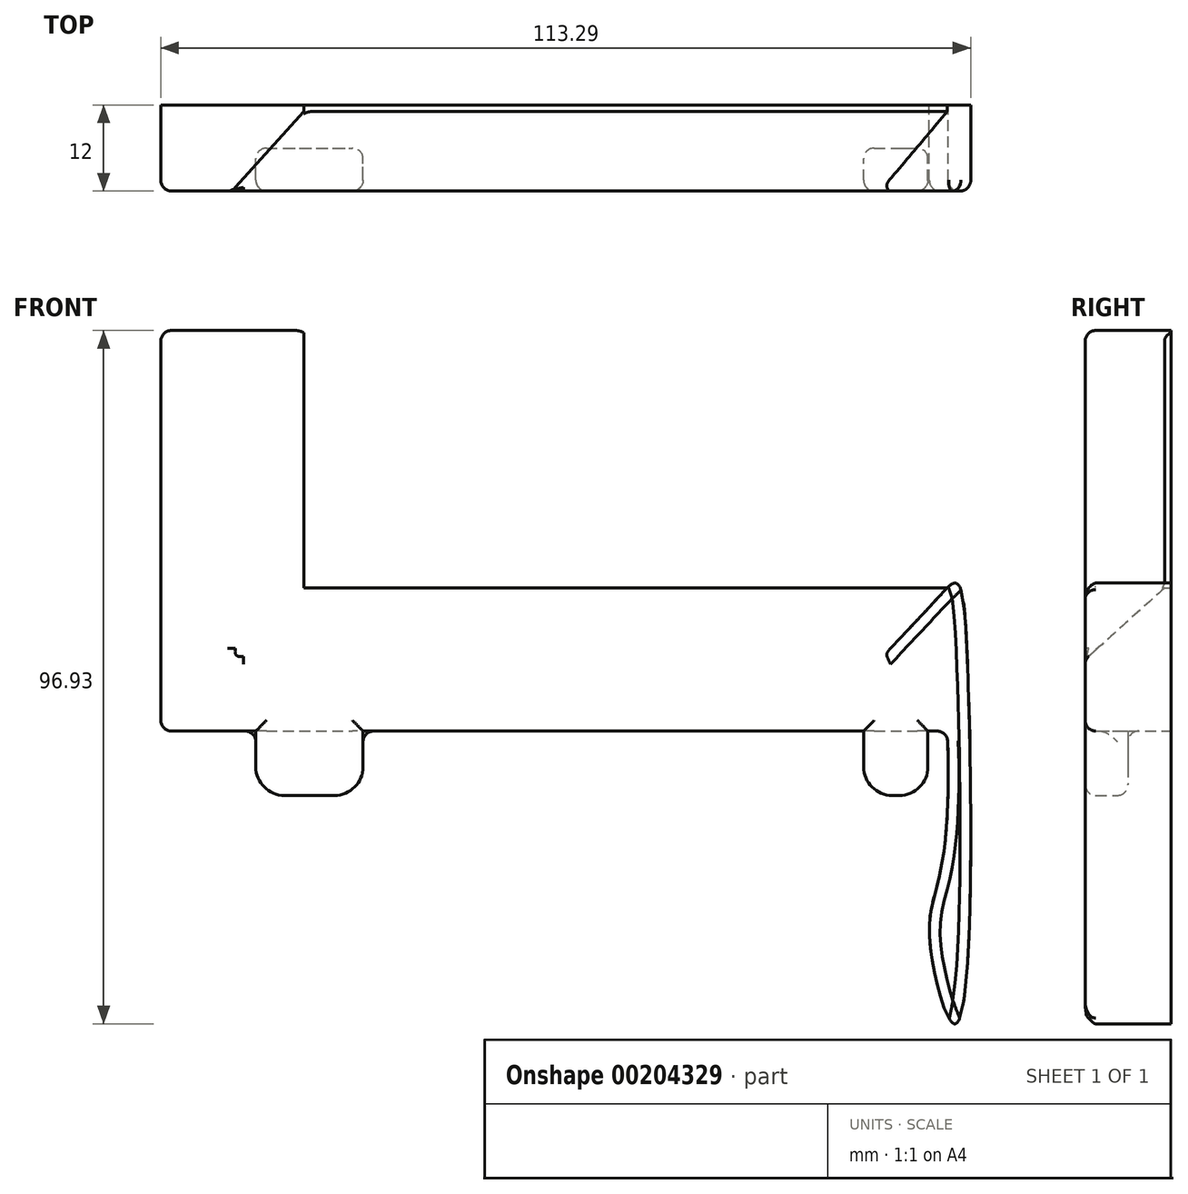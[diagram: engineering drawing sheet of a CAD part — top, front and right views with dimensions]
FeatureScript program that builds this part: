
annotation { "Feature Type Name" : "Feature", "Feature Type Description" : "" }
export const myFeature = defineFeature(function(context is Context, id is Id, definition is map)
    precondition{}
    {
        {
            var Q0;
            Q0=qCreatedBy(makeId("Front.planeOp"),FACE);
            var sketch = newSketch(context, id + "F0", { "sketchPlane" : qUnion([Q0])});
            skLineSegment(sketch, "E0", {"start": v(-34.63, 49.53) * mm, "end": v(-34.63, -6.47) * mm});
            skLineSegment(sketch, "E1", {"start": v(-34.63, -6.47) * mm, "end": v(75.37, -6.47) * mm});
            skLineSegment(sketch, "E2", {"start": v(75.37, -6.47) * mm, "end": v(75.37, 13.53) * mm});
            skLineSegment(sketch, "E3", {"start": v(75.37, 13.53) * mm, "end": v(-14.63, 13.53) * mm});
            skLineSegment(sketch, "E4", {"start": v(-14.63, 13.53) * mm, "end": v(-14.63, 49.53) * mm});
            skLineSegment(sketch, "E5", {"start": v(-14.63, 49.53) * mm, "end": v(-34.63, 49.53) * mm});
            skLineSegment(sketch, "E6", {"start": v(-21.33, -6.47) * mm, "end": v(-21.33, -15.47) * mm});
            skLineSegment(sketch, "E7", {"start": v(-21.33, -15.47) * mm, "end": v(-6.33, -15.47) * mm});
            skLineSegment(sketch, "E8", {"start": v(-6.33, -15.47) * mm, "end": v(-6.33, -6.47) * mm});
            skLineSegment(sketch, "E9", {"start": v(72.67, -6.47) * mm, "end": v(72.67, -15.47) * mm});
            skLineSegment(sketch, "E10", {"start": v(63.67, -15.47) * mm, "end": v(72.67, -15.47) * mm});
            skLineSegment(sketch, "E11", {"start": v(63.67, -15.47) * mm, "end": v(63.67, -6.47) * mm});
            skLineSegment(sketch, "E12.bottom", {"start": v(-16.83, -6.47) * mm, "end": v(-10.83, -6.47) * mm});
            skLineSegment(sketch, "E12.top", {"start": v(-16.83, -15.47) * mm, "end": v(-10.83, -15.47) * mm});
            skLineSegment(sketch, "E12.left", {"start": v(-16.83, -6.47) * mm, "end": v(-16.83, -15.47) * mm});
            skLineSegment(sketch, "E12.right", {"start": v(-10.83, -6.47) * mm, "end": v(-10.83, -15.47) * mm});
            skLineSegment(sketch, "E13.bottom", {"start": v(65.17, -6.47) * mm, "end": v(71.17, -6.47) * mm});
            skLineSegment(sketch, "E13.top", {"start": v(65.17, -15.47) * mm, "end": v(71.17, -15.47) * mm});
            skLineSegment(sketch, "E13.left", {"start": v(65.17, -6.47) * mm, "end": v(65.17, -15.47) * mm});
            skLineSegment(sketch, "E13.right", {"start": v(71.17, -6.47) * mm, "end": v(71.17, -15.47) * mm});
            skLineSegment(sketch, "E14.bottom", {"start": v(-21.33, -6.47) * mm, "end": v(-6.33, -6.47) * mm});
            skLineSegment(sketch, "E14.top", {"start": v(-21.33, -10.67) * mm, "end": v(-6.33, -10.67) * mm});
            skLineSegment(sketch, "E14.left", {"start": v(-21.33, -6.47) * mm, "end": v(-21.33, -10.67) * mm});
            skLineSegment(sketch, "E14.right", {"start": v(-6.33, -6.47) * mm, "end": v(-6.33, -10.67) * mm});
            skLineSegment(sketch, "E15.bottom", {"start": v(63.67, -6.47) * mm, "end": v(72.67, -6.47) * mm});
            skLineSegment(sketch, "E15.top", {"start": v(63.67, -10.67) * mm, "end": v(72.67, -10.67) * mm});
            skLineSegment(sketch, "E15.left", {"start": v(63.67, -6.47) * mm, "end": v(63.67, -10.67) * mm});
            skLineSegment(sketch, "E15.right", {"start": v(72.67, -6.47) * mm, "end": v(72.67, -10.67) * mm});
            skFitSpline(sketch, "E16", {"points": [v(75.37, 13.53) * mm, v(78.02, 6.78) * mm, v(76.56, -47.38) * mm, v(72.89, -35.3) * mm, v(75.37, -6.47) * mm], "startDerivative": vector(42.22, 45.02) * mm, "endDerivative": vector(-9.37, 234.27) * mm});
            skSolve(sketch);
        }
        {
            var Q0;
            {var subQ4=sQuery(id+"F0.wireOp",EDGE,"E0");Q0=makeQuery(id+"F0.imprint","IMPRINT",FACE,{"disambiguationData":[TD([[makeQuery(id+"F0.imprint","IMPRINT",EDGE,{"derivedFrom":subQ4}),1.0]])]});}
            var Q1;
            {var subQ0=sQuery(id+"F0.wireOp",EDGE,"E6");Q1=makeQuery(id+"F0.imprint","IMPRINT",FACE,{"disambiguationData":[TD([[makeQuery(id+"F0.imprint","IMPRINT",EDGE,{"derivedFrom":subQ0}),1.0]])]});}
            var Q2;
            {var subQ0=sQuery(id+"F0.wireOp",EDGE,"E9");Q2=makeQuery(id+"F0.imprint","IMPRINT",FACE,{"disambiguationData":[TD([[makeQuery(id+"F0.imprint","IMPRINT",EDGE,{"derivedFrom":subQ0}),-1.0]])]});}
            var Q3;
            Q3=makeQuery(id+"F0.imprint","IMPRINT",FACE,{"disambiguationData":[TD([[makeQuery(id+"F0.imprint","IMPRINT",EDGE,{"derivedFrom":sQuery(id+"F0.wireOp",EDGE,"E12.bottom")}),-1.0]])]});
            var Q4;
            Q4=makeQuery(id+"F0.imprint","IMPRINT",FACE,{"disambiguationData":[TD([[makeQuery(id+"F0.imprint","IMPRINT",EDGE,{"derivedFrom":sQuery(id+"F0.wireOp",EDGE,"E13.bottom")}),-1.0]])]});
            var Q5;
            {var subQ0=sQuery(id+"F0.wireOp",EDGE,"E8");Q5=makeQuery(id+"F0.imprint","IMPRINT",FACE,{"disambiguationData":[TD([[makeQuery(id+"F0.imprint","IMPRINT",EDGE,{"derivedFrom":subQ0}),1.0]])]});}
            var Q6;
            {var subQ0=sQuery(id+"F0.wireOp",EDGE,"E11");Q6=makeQuery(id+"F0.imprint","IMPRINT",FACE,{"disambiguationData":[TD([[makeQuery(id+"F0.imprint","IMPRINT",EDGE,{"derivedFrom":subQ0}),-1.0]])]});}
            var Q7;
            {var subQ0=sQuery(id+"F0.wireOp",EDGE,"E14.bottom");var subQ1=sQuery(id+"F0.wireOp",EDGE,"E12.left");var subQ2=makeQuery(id+"F0.imprint","INTERSECT",VERTEX,{"derivedFrom":[subQ1,subQ0]});Q7=makeQuery(id+"F0.imprint","IMPRINT",FACE,{"disambiguationData":[TD([[makeQuery(id+"F0.imprint","IMPRINT",EDGE,{"disambiguationData":[TD([[subQ2,-1.0]])],"derivedFrom":subQ1}),1.0]])]});}
            var Q8;
            {var subQ0=sQuery(id+"F0.wireOp",EDGE,"E12.top");Q8=makeQuery(id+"F0.imprint","IMPRINT",FACE,{"disambiguationData":[TD([[makeQuery(id+"F0.imprint","IMPRINT",EDGE,{"derivedFrom":subQ0}),1.0]])]});}
            var Q9;
            {var subQ5=sQuery(id+"F0.wireOp",EDGE,"E14.right");Q9=makeQuery(id+"F0.imprint","IMPRINT",FACE,{"disambiguationData":[TD([[makeQuery(id+"F0.imprint","IMPRINT",EDGE,{"derivedFrom":subQ5}),-1.0]])]});}
            var Q10;
            {var subQ5=sQuery(id+"F0.wireOp",EDGE,"E14.left");Q10=makeQuery(id+"F0.imprint","IMPRINT",FACE,{"disambiguationData":[TD([[makeQuery(id+"F0.imprint","IMPRINT",EDGE,{"derivedFrom":subQ5}),1.0]])]});}
            var Q11;
            {var subQ0=sQuery(id+"F0.wireOp",EDGE,"E15.bottom");var subQ1=sQuery(id+"F0.wireOp",EDGE,"E13.left");var subQ2=makeQuery(id+"F0.imprint","INTERSECT",VERTEX,{"derivedFrom":[subQ1,subQ0]});Q11=makeQuery(id+"F0.imprint","IMPRINT",FACE,{"disambiguationData":[TD([[makeQuery(id+"F0.imprint","IMPRINT",EDGE,{"disambiguationData":[TD([[subQ2,-1.0]])],"derivedFrom":subQ1}),1.0]])]});}
            var Q12;
            {var subQ0=sQuery(id+"F0.wireOp",EDGE,"E13.top");Q12=makeQuery(id+"F0.imprint","IMPRINT",FACE,{"disambiguationData":[TD([[makeQuery(id+"F0.imprint","IMPRINT",EDGE,{"derivedFrom":subQ0}),1.0]])]});}
            var Q13;
            {var subQ5=sQuery(id+"F0.wireOp",EDGE,"E15.right");Q13=makeQuery(id+"F0.imprint","IMPRINT",FACE,{"disambiguationData":[TD([[makeQuery(id+"F0.imprint","IMPRINT",EDGE,{"derivedFrom":subQ5}),-1.0]])]});}
            var Q14;
            {var subQ5=sQuery(id+"F0.wireOp",EDGE,"E15.left");Q14=makeQuery(id+"F0.imprint","IMPRINT",FACE,{"disambiguationData":[TD([[makeQuery(id+"F0.imprint","IMPRINT",EDGE,{"derivedFrom":subQ5}),1.0]])]});}
            var Q15;
            Q15=makeQuery(id+"F0.imprint","IMPRINT",FACE,{"disambiguationData":[TD([[makeQuery(id+"F0.imprint","IMPRINT",EDGE,{"derivedFrom":sQuery(id+"F0.wireOp",EDGE,"E2")}),-1.0]])]});
            extrude(context, id + "F1", {"entities" : qUnion([Q0, Q1, Q2, Q3, Q4, Q5, Q6, Q7, Q8, Q9, Q10, Q11, Q12, Q13, Q14, Q15]), "depth" : 12 * mm});
        }
        {
            var Q0;
            Q0=makeQuery(id+"F1.opExtrude","CAP_EDGE",EDGE,{"disambiguationData":[OSD([sQuery(id+"F0.wireOp",EDGE,"E4")])],"isStart":false});
            var Q1;
            Q1=makeQuery(id+"F1.opExtrude","CAP_EDGE",EDGE,{"disambiguationData":[OSD([sQuery(id+"F0.wireOp",EDGE,"E3")])],"isStart":false});
            chamfer(context, id + "F2", {"entities" : qUnion([Q0, Q1]), "chamferType" : ChamferType.OFFSET_ANGLE, "width" : 10 * mm, "oppositeDirection" : false, "angle" : 48 * degree});
        }
        {
            var Q0;
            {var subQ0=sQuery(id+"F0.wireOp",EDGE,"E12.top");Q0=makeQuery(id+"F0.imprint","IMPRINT",FACE,{"disambiguationData":[TD([[makeQuery(id+"F0.imprint","IMPRINT",EDGE,{"derivedFrom":subQ0}),1.0]])]});}
            var Q1;
            {var subQ0=sQuery(id+"F0.wireOp",EDGE,"E15.bottom");var subQ1=sQuery(id+"F0.wireOp",EDGE,"E13.left");var subQ2=makeQuery(id+"F0.imprint","INTERSECT",VERTEX,{"derivedFrom":[subQ1,subQ0]});Q1=makeQuery(id+"F0.imprint","IMPRINT",FACE,{"disambiguationData":[TD([[makeQuery(id+"F0.imprint","IMPRINT",EDGE,{"disambiguationData":[TD([[subQ2,-1.0]])],"derivedFrom":subQ1}),1.0]])]});}
            var Q2;
            {var subQ0=sQuery(id+"F0.wireOp",EDGE,"E14.bottom");var subQ1=sQuery(id+"F0.wireOp",EDGE,"E12.left");var subQ2=makeQuery(id+"F0.imprint","INTERSECT",VERTEX,{"derivedFrom":[subQ1,subQ0]});Q2=makeQuery(id+"F0.imprint","IMPRINT",FACE,{"disambiguationData":[TD([[makeQuery(id+"F0.imprint","IMPRINT",EDGE,{"disambiguationData":[TD([[subQ2,-1.0]])],"derivedFrom":subQ1}),1.0]])]});}
            var Q3;
            {var subQ5=sQuery(id+"F0.wireOp",EDGE,"E14.left");Q3=makeQuery(id+"F0.imprint","IMPRINT",FACE,{"disambiguationData":[TD([[makeQuery(id+"F0.imprint","IMPRINT",EDGE,{"derivedFrom":subQ5}),1.0]])]});}
            var Q4;
            {var subQ5=sQuery(id+"F0.wireOp",EDGE,"E14.right");Q4=makeQuery(id+"F0.imprint","IMPRINT",FACE,{"disambiguationData":[TD([[makeQuery(id+"F0.imprint","IMPRINT",EDGE,{"derivedFrom":subQ5}),-1.0]])]});}
            var Q5;
            {var subQ5=sQuery(id+"F0.wireOp",EDGE,"E15.left");Q5=makeQuery(id+"F0.imprint","IMPRINT",FACE,{"disambiguationData":[TD([[makeQuery(id+"F0.imprint","IMPRINT",EDGE,{"derivedFrom":subQ5}),1.0]])]});}
            var Q6;
            {var subQ5=sQuery(id+"F0.wireOp",EDGE,"E15.right");Q6=makeQuery(id+"F0.imprint","IMPRINT",FACE,{"disambiguationData":[TD([[makeQuery(id+"F0.imprint","IMPRINT",EDGE,{"derivedFrom":subQ5}),-1.0]])]});}
            var Q7;
            {var subQ0=sQuery(id+"F0.wireOp",EDGE,"E8");Q7=makeQuery(id+"F0.imprint","IMPRINT",FACE,{"disambiguationData":[TD([[makeQuery(id+"F0.imprint","IMPRINT",EDGE,{"derivedFrom":subQ0}),1.0]])]});}
            var Q8;
            {var subQ0=sQuery(id+"F0.wireOp",EDGE,"E6");Q8=makeQuery(id+"F0.imprint","IMPRINT",FACE,{"disambiguationData":[TD([[makeQuery(id+"F0.imprint","IMPRINT",EDGE,{"derivedFrom":subQ0}),1.0]])]});}
            var Q9;
            {var subQ0=sQuery(id+"F0.wireOp",EDGE,"E13.top");Q9=makeQuery(id+"F0.imprint","IMPRINT",FACE,{"disambiguationData":[TD([[makeQuery(id+"F0.imprint","IMPRINT",EDGE,{"derivedFrom":subQ0}),1.0]])]});}
            var Q10;
            {var subQ0=sQuery(id+"F0.wireOp",EDGE,"E11");Q10=makeQuery(id+"F0.imprint","IMPRINT",FACE,{"disambiguationData":[TD([[makeQuery(id+"F0.imprint","IMPRINT",EDGE,{"derivedFrom":subQ0}),-1.0]])]});}
            var Q11;
            {var subQ0=sQuery(id+"F0.wireOp",EDGE,"E9");Q11=makeQuery(id+"F0.imprint","IMPRINT",FACE,{"disambiguationData":[TD([[makeQuery(id+"F0.imprint","IMPRINT",EDGE,{"derivedFrom":subQ0}),-1.0]])]});}
            extrude(context, id + "F3", {"entities" : qUnion([Q0, Q1, Q2, Q3, Q4, Q5, Q6, Q7, Q8, Q9, Q10, Q11]), "operationType" : NewBodyOperationType.REMOVE, "depth" : 6 * mm});
        }
        {
            var Q0;
            Q0=makeQuery(id+"F1.opExtrude","SWEPT_EDGE",EDGE,{"disambiguationData":[OSD([sQuery(id+"F0.wireOp",EDGE,"E6"),sQuery(id+"F0.wireOp",EDGE,"E7")])]});
            var Q1;
            Q1=makeQuery(id+"F1.opExtrude","SWEPT_EDGE",EDGE,{"disambiguationData":[OSD([sQuery(id+"F0.wireOp",EDGE,"E7"),sQuery(id+"F0.wireOp",EDGE,"E8")])]});
            var Q2;
            Q2=makeQuery(id+"F1.opExtrude","SWEPT_EDGE",EDGE,{"disambiguationData":[OSD([sQuery(id+"F0.wireOp",EDGE,"E10"),sQuery(id+"F0.wireOp",EDGE,"E11")])]});
            var Q3;
            Q3=makeQuery(id+"F1.opExtrude","SWEPT_EDGE",EDGE,{"disambiguationData":[OSD([sQuery(id+"F0.wireOp",EDGE,"E9"),sQuery(id+"F0.wireOp",EDGE,"E10")])]});
            fillet(context, id + "F4", {"entities" : qUnion([Q0, Q1, Q2, Q3]), "radius" : 4 * mm, "tangentPropagation" : true, "allowEdgeOverflow" : false});
        }
        {
            var Q0;
            Q0=makeQuery(id+"F1.opExtrude","CAP_FACE",FACE,{"disambiguationData":[OSD([sQuery(id+"F0.wireOp",EDGE,"E0"),sQuery(id+"F0.wireOp",EDGE,"E1"),sQuery(id+"F0.wireOp",EDGE,"E2"),sQuery(id+"F0.wireOp",EDGE,"E3"),sQuery(id+"F0.wireOp",EDGE,"E4"),sQuery(id+"F0.wireOp",EDGE,"E5"),sQuery(id+"F0.wireOp",EDGE,"E6"),sQuery(id+"F0.wireOp",EDGE,"E7"),sQuery(id+"F0.wireOp",EDGE,"E8"),sQuery(id+"F0.wireOp",EDGE,"E9"),sQuery(id+"F0.wireOp",EDGE,"E10"),sQuery(id+"F0.wireOp",EDGE,"E11"),sQuery(id+"F0.wireOp",EDGE,"E12.top"),sQuery(id+"F0.wireOp",EDGE,"E13.top"),sQuery(id+"F0.wireOp",EDGE,"E14.left"),sQuery(id+"F0.wireOp",EDGE,"E14.right"),sQuery(id+"F0.wireOp",EDGE,"E15.left"),sQuery(id+"F0.wireOp",EDGE,"E15.right")])],"isStart":false});
            var Q1;
            Q1=makeQuery(id+"F1.opExtrude","SWEPT_EDGE",EDGE,{"disambiguationData":[OSD([sQuery(id+"F0.wireOp",EDGE,"E0"),sQuery(id+"F0.wireOp",EDGE,"E1")])]});
            var Q2;
            Q2=makeQuery(id+"F1.opExtrude","SWEPT_EDGE",EDGE,{"disambiguationData":[OSD([sQuery(id+"F0.wireOp",EDGE,"E0"),sQuery(id+"F0.wireOp",EDGE,"E5")])]});
            var Q3;
            Q3=makeQuery(id+"F1.opExtrude","SWEPT_EDGE",EDGE,{"disambiguationData":[OSD([sQuery(id+"F0.wireOp",EDGE,"E1"),sQuery(id+"F0.wireOp",EDGE,"E2")])]});
            var Q4;
            Q4=makeQuery(id+"F3.boolean.opBoolean","COPY",FACE,{"derivedFrom":makeQuery(id+"F3.opExtrude","CAP_FACE",FACE,{"disambiguationData":[OSD([sQuery(id+"F0.wireOp",EDGE,"E6"),sQuery(id+"F0.wireOp",EDGE,"E7"),sQuery(id+"F0.wireOp",EDGE,"E8"),sQuery(id+"F0.wireOp",EDGE,"E12.top"),sQuery(id+"F0.wireOp",EDGE,"E14.bottom"),sQuery(id+"F0.wireOp",EDGE,"E14.left"),sQuery(id+"F0.wireOp",EDGE,"E14.right")])],"isStart":false})});
            var Q5;
            {var subQ0=sQuery(id+"F0.wireOp",EDGE,"E10");var subQ1=sQuery(id+"F0.wireOp",EDGE,"E9");Q5=makeQuery(id+"F4.opFillet","BLEND_EDGE",EDGE,{"blendedFrom":[makeQuery(id+"F1.opExtrude","SWEPT_EDGE",EDGE,{"disambiguationData":[OSD([subQ1,subQ0])]}),makeQuery(id+"F3.boolean.opBoolean","COPY",FACE,{"derivedFrom":makeQuery(id+"F3.opExtrude","CAP_FACE",FACE,{"disambiguationData":[OSD([subQ1,subQ0,sQuery(id+"F0.wireOp",EDGE,"E11"),sQuery(id+"F0.wireOp",EDGE,"E13.top"),sQuery(id+"F0.wireOp",EDGE,"E15.bottom"),sQuery(id+"F0.wireOp",EDGE,"E15.left"),sQuery(id+"F0.wireOp",EDGE,"E15.right")])],"isStart":false})})],"blendedInto":[makeQuery(id+"F3.boolean.opBoolean","COPY",FACE,{"derivedFrom":makeQuery(id+"F3.opExtrude","CAP_FACE",FACE,{"disambiguationData":[OSD([subQ1,subQ0,sQuery(id+"F0.wireOp",EDGE,"E11"),sQuery(id+"F0.wireOp",EDGE,"E13.top"),sQuery(id+"F0.wireOp",EDGE,"E15.bottom"),sQuery(id+"F0.wireOp",EDGE,"E15.left"),sQuery(id+"F0.wireOp",EDGE,"E15.right")])],"isStart":false})})]});}
            var Q6;
            Q6=makeQuery(id+"F2.opChamfer","BLEND_EDGE",EDGE,{"blendedFrom":[makeQuery(id+"F1.opExtrude","CAP_EDGE",EDGE,{"disambiguationData":[OSD([sQuery(id+"F0.wireOp",EDGE,"E4")])],"isStart":false}),makeQuery(id+"F1.opExtrude","SWEPT_FACE",FACE,{"disambiguationData":[OSD([sQuery(id+"F0.wireOp",EDGE,"E5")])]})],"blendedInto":[makeQuery(id+"F1.opExtrude","SWEPT_FACE",FACE,{"disambiguationData":[OSD([sQuery(id+"F0.wireOp",EDGE,"E5")])]})]});
            var Q7;
            Q7=makeQuery(id+"F2.opChamfer","BLEND_EDGE",EDGE,{"blendedFrom":[makeQuery(id+"F1.opExtrude","CAP_EDGE",EDGE,{"disambiguationData":[OSD([sQuery(id+"F0.wireOp",EDGE,"E3")])],"isStart":false}),makeQuery(id+"F1.opExtrude","SWEPT_FACE",FACE,{"disambiguationData":[OSD([sQuery(id+"F0.wireOp",EDGE,"E2")])]})],"blendedInto":[makeQuery(id+"F1.opExtrude","SWEPT_FACE",FACE,{"disambiguationData":[OSD([sQuery(id+"F0.wireOp",EDGE,"E2")])]})]});
            var Q8;
            Q8=makeQuery(id+"F2.opChamfer","BLEND_EDGE",EDGE,{"blendedFrom":[makeQuery(id+"F1.opExtrude","CAP_EDGE",EDGE,{"disambiguationData":[OSD([sQuery(id+"F0.wireOp",EDGE,"E3")])],"isStart":false}),makeQuery(id+"F1.opExtrude","CAP_EDGE",EDGE,{"disambiguationData":[OSD([sQuery(id+"F0.wireOp",EDGE,"E4")])],"isStart":false})],"blendedInto":[]});
            fillet(context, id + "F5", {"entities" : qUnion([Q0, Q1, Q2, Q3, Q4, Q5, Q6, Q7, Q8]), "radius" : 1.5 * mm, "tangentPropagation" : true, "allowEdgeOverflow" : false});
        }
    });
